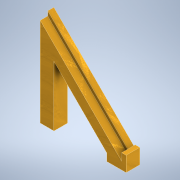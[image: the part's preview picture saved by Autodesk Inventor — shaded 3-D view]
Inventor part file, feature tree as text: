
AUTODESK INVENTOR PART (.ipt)
format: ipt  version: 2022.2 (Build 262287010, 287A)  size: 156,672 bytes
history: native  units: in
note: dims shown in document units (in); Inventor stores cm internally (conversion verified against a paired STEP export)
features: extrude x6, sketch x6, other x1, plane x1
ambient origin geometry x8: Origin, YZ Plane, XZ Plane, XY Plane, X Axis, Y Axis, Z Axis, Center Point
bodies: Body1 (feature_tree)
feature tree (14):
  other  "Sólido1"
  extrude  "Extrusión1"  TaperAngle=45.0deg  [1 undecoded]
  extrude  "Extrusión2"  Depth=0.1181in
  extrude  "Extrusión3"  Depth=0.3543in TaperAngle=0.0deg
  extrude  "Extrusión4"  Depth=1.378in
  extrude  "Extrusión5"  Depth=0.5906in TaperAngle=0.0deg
  extrude  "Extrusión6"  Depth=0.1969in TaperAngle=0.0deg
  plane  "Plano de trabajo1"
  sketch  "Boceto1"  dims[d0=2.126in d2=45.0deg]
  sketch  "Boceto2"  dims[d3=0.1969in d4=0.0in d9=0.1181in]
  sketch  "Boceto4"  dims[d10=0.1969in d11=0.3543in d12=0.0in]
  sketch  "Boceto5"  dims[d17=0.1575in d18=0.0in d19=1.378in]
  sketch  "Boceto6"  dims[d20=135.0deg d21=0.5906in d22=0.0in]
  sketch  "Boceto7"  dims[d24=45.0deg d25=0.1969in d26=0.0in d27=0.1969in d28=0.0in d29=-0.7874in d15=0.0197in d16=0.0344in]
note: 1 required parameter value undecoded (feature->parameter linkage not recoverable at this tier; creation-order binding heuristic only, values carry confidence <= 0.55)
